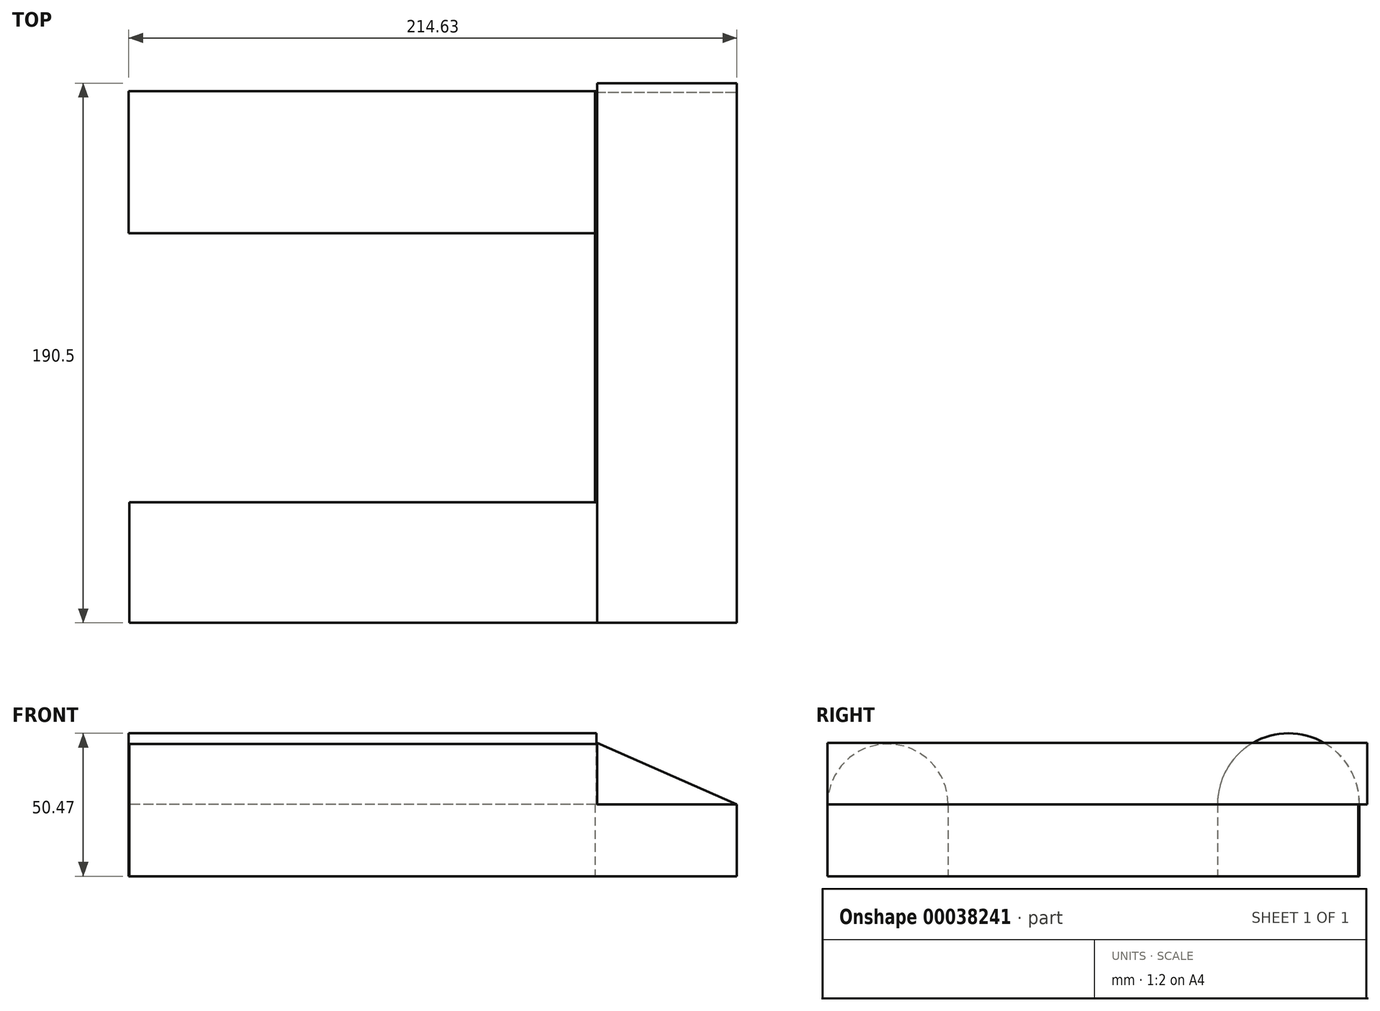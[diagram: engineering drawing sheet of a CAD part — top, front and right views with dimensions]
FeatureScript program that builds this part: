
annotation { "Feature Type Name" : "Feature", "Feature Type Description" : "" }
export const myFeature = defineFeature(function(context is Context, id is Id, definition is map)
    precondition{}
    {
        {
            var Q0;
            Q0=qCreatedBy(makeId("Top.planeOp"),FACE);
            var sketch = newSketch(context, id + "F0", { "sketchPlane" : qUnion([Q0])});
            skLineSegment(sketch, "E0.rect.bottom", {"start": v(35.07, -25.07) * mm, "end": v(-129.5, -25.07) * mm});
            skLineSegment(sketch, "E0.rect.top", {"start": v(35.07, 25.07) * mm, "end": v(-129.5, 25.07) * mm});
            skLineSegment(sketch, "E0.rect.left", {"start": v(35.07, -25.07) * mm, "end": v(35.07, 25.07) * mm});
            skLineSegment(sketch, "E0.rect.right", {"start": v(-129.5, -25.07) * mm, "end": v(-129.5, 25.07) * mm});
            skPoint(sketch, "E0.rect.middle", {"position": v(-47.22, 0) * mm});
            skSolve(sketch);
        }
        {
            var Q0;
            Q0=makeQuery(id+"F0.imprint","IMPRINT",FACE,{"disambiguationData":[TD([[makeQuery(id+"F0.imprint","IMPRINT",EDGE,{"derivedFrom":sQuery(id+"F0.wireOp",EDGE,"E0.rect.bottom")}),-1.0]])]});
            extrude(context, id + "F1", {"entities" : qUnion([Q0]), "depth" : 25.4 * mm});
        }
        {
            var Q0;
            Q0=qCreatedBy(makeId("Top.planeOp"),FACE);
            var sketch = newSketch(context, id + "F2", { "sketchPlane" : qUnion([Q0])});
            skLineSegment(sketch, "E1.bottom", {"start": v(35.08, 24.6) * mm, "end": v(85.13, 24.6) * mm});
            skLineSegment(sketch, "E1.top", {"start": v(35.08, -120.13) * mm, "end": v(85.13, -120.13) * mm});
            skLineSegment(sketch, "E1.left", {"start": v(35.08, 24.6) * mm, "end": v(35.08, -120.13) * mm});
            skLineSegment(sketch, "E1.right", {"start": v(85.13, 24.6) * mm, "end": v(85.13, -120.13) * mm});
            skLineSegment(sketch, "E2.bottom", {"start": v(85.13, -120.13) * mm, "end": v(-129.26, -120.13) * mm});
            skLineSegment(sketch, "E2.top", {"start": v(85.13, -162.67) * mm, "end": v(-129.26, -162.67) * mm});
            skLineSegment(sketch, "E2.left", {"start": v(85.13, -120.13) * mm, "end": v(85.13, -162.67) * mm});
            skLineSegment(sketch, "E2.right", {"start": v(-129.26, -120.13) * mm, "end": v(-129.26, -162.67) * mm});
            skSolve(sketch);
        }
        {
            var Q0;
            Q0 = qSketchRegion(id + "F2", true);
            var Q1;
            Q1=makeQuery(id+"F2.imprint","IMPRINT",FACE,{"disambiguationData":[TD([[makeQuery(id+"F2.imprint","IMPRINT",EDGE,{"derivedFrom":sQuery(id+"F2.wireOp",EDGE,"E1.bottom")}),-1.0]])]});
            var Q2;
            Q2=makeQuery(id+"F2.imprint","IMPRINT",FACE,{"disambiguationData":[TD([[makeQuery(id+"F2.imprint","IMPRINT",EDGE,{"derivedFrom":sQuery(id+"F2.wireOp",EDGE,"E2.top")}),-1.0]])]});
            extrude(context, id + "F3", {"entities" : qUnion([Q0, Q1, Q2]), "depth" : 25.4 * mm});
        }
        {
            var Q0;
            Q0=makeQuery(id+"F3.opExtrude","SWEPT_FACE",FACE,{"disambiguationData":[OSD([sQuery(id+"F2.wireOp",EDGE,"E2.right")])]});
            var sketch = newSketch(context, id + "F4", { "sketchPlane" : qUnion([Q0])});
            skArc(sketch, "E3", {"start": v(162.67, 25.4) * mm, "mid": v(141.4, 46.67) * mm, "end": v(120.13, 25.4) * mm});
            skSolve(sketch);
        }
        {
            var Q0;
            Q0=makeQuery(id+"F4.imprint","IMPRINT",FACE,{"disambiguationData":[TD([[makeQuery(id+"F4.imprint","IMPRINT",EDGE,{"derivedFrom":sQuery(id+"F4.wireOp",EDGE,"E3")}),1.0]])]});
            extrude(context, id + "F5", {"entities" : qUnion([Q0]), "operationType" : NewBodyOperationType.ADD, "oppositeDirection" : true, "depth" : 165.1 * mm});
        }
        {
            var Q0;
            Q0=makeQuery(id+"F3.opExtrude","SWEPT_FACE",FACE,{"disambiguationData":[OSD([sQuery(id+"F2.wireOp",EDGE,"E2.top")])]});
            var sketch = newSketch(context, id + "F6", { "sketchPlane" : qUnion([Q0])});
            skLineSegment(sketch, "E4", {"start": v(35.84, 25.4) * mm, "end": v(35.84, 47.06) * mm});
            skLineSegment(sketch, "E5", {"start": v(35.84, 47.06) * mm, "end": v(85.13, 25.4) * mm});
            skLineSegment(sketch, "E6", {"start": v(85.13, 25.4) * mm, "end": v(35.84, 25.4) * mm});
            skSolve(sketch);
        }
        {
            var Q0;
            Q0=makeQuery(id+"F6.imprint","IMPRINT",FACE,{"disambiguationData":[TD([[makeQuery(id+"F6.imprint","IMPRINT",EDGE,{"derivedFrom":sQuery(id+"F6.wireOp",EDGE,"E4")}),-1.0]])]});
            extrude(context, id + "F7", {"entities" : qUnion([Q0]), "oppositeDirection" : true, "depth" : 190.5 * mm});
        }
        {
            var Q0;
            Q0=makeQuery(id+"F1.opExtrude","SWEPT_FACE",FACE,{"disambiguationData":[OSD([sQuery(id+"F0.wireOp",EDGE,"E0.rect.right")])]});
            var sketch = newSketch(context, id + "F8", { "sketchPlane" : qUnion([Q0])});
            skArc(sketch, "E7", {"start": v(25.07, 25.4) * mm, "mid": v(0, 50.47) * mm, "end": v(-25.07, 25.4) * mm});
            skLineSegment(sketch, "E8", {"start": v(25.07, 25.4) * mm, "end": v(-25.07, 25.4) * mm});
            skSolve(sketch);
        }
        {
            var Q0;
            Q0=makeQuery(id+"F8.imprint","IMPRINT",FACE,{"disambiguationData":[TD([[makeQuery(id+"F8.imprint","IMPRINT",EDGE,{"derivedFrom":sQuery(id+"F8.wireOp",EDGE,"E7")}),1.0]])]});
            extrude(context, id + "F9", {"entities" : qUnion([Q0]), "oppositeDirection" : true, "depth" : 165.1 * mm});
        }
    });
